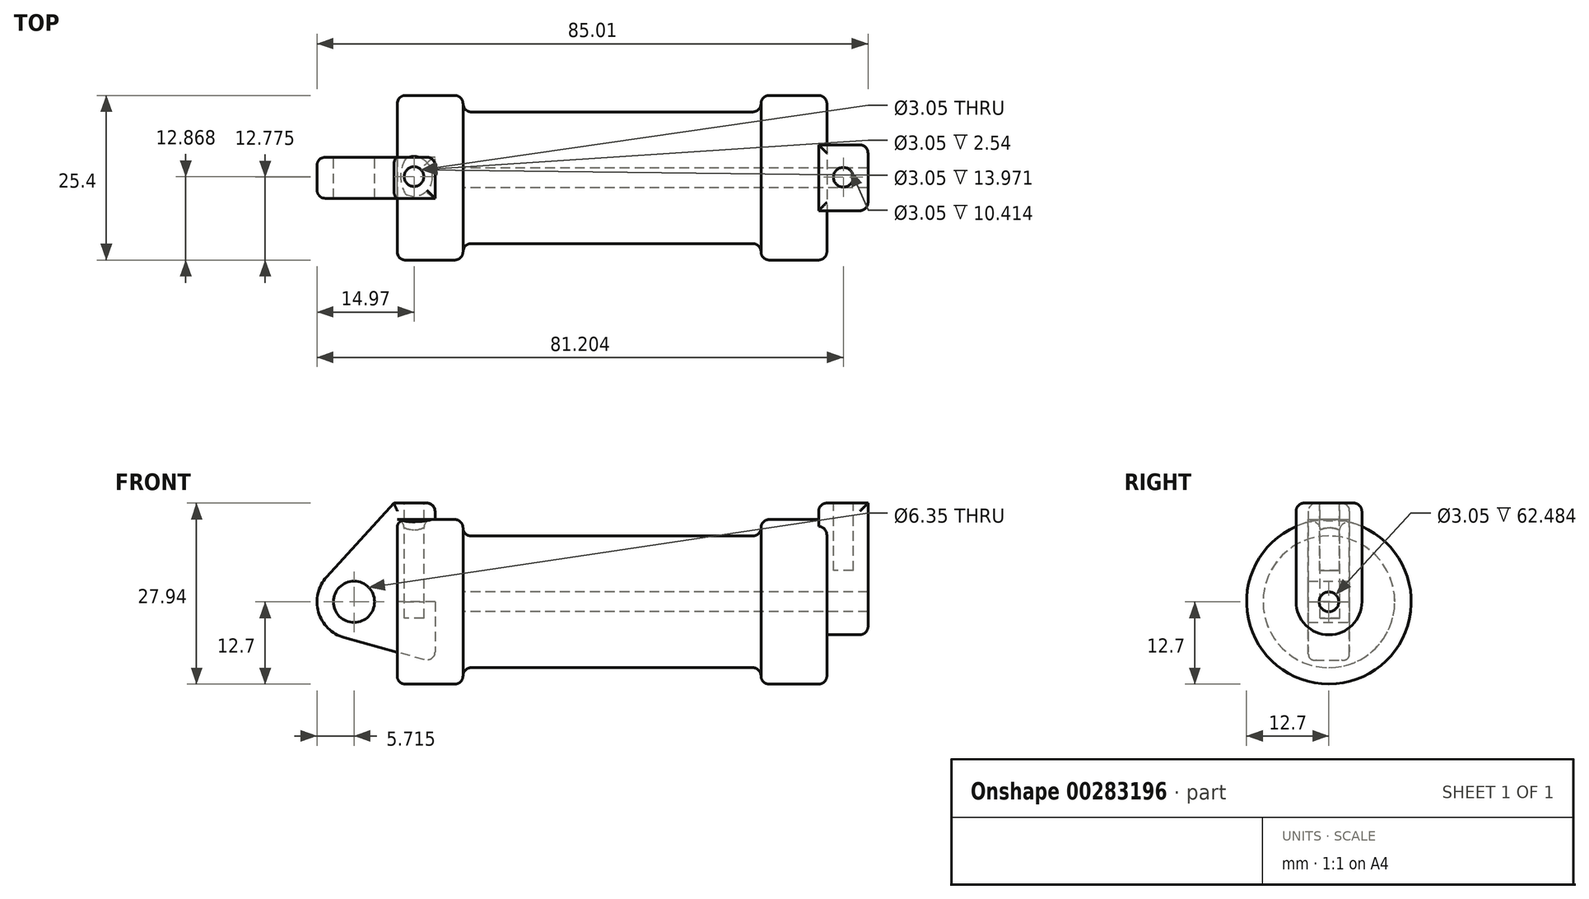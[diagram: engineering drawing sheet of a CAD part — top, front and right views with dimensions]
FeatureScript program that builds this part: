
annotation { "Feature Type Name" : "Feature", "Feature Type Description" : "" }
export const myFeature = defineFeature(function(context is Context, id is Id, definition is map)
    precondition{}
    {
        {
            var Q0;
            Q0=qCreatedBy(makeId("Front.planeOp"),FACE);
            var sketch = newSketch(context, id + "F0", { "sketchPlane" : qUnion([Q0])});
            skLineSegment(sketch, "E0", {"start": v(0, 0) * mm, "end": v(0, 12.7) * mm});
            skLineSegment(sketch, "E1", {"start": v(0, 12.7) * mm, "end": v(10.16, 12.7) * mm});
            skLineSegment(sketch, "E2", {"start": v(10.16, 12.7) * mm, "end": v(10.16, 10.16) * mm});
            skLineSegment(sketch, "E3", {"start": v(10.16, 10.16) * mm, "end": v(56.13, 10.16) * mm});
            skLineSegment(sketch, "E4", {"start": v(56.13, 10.16) * mm, "end": v(56.13, 12.7) * mm});
            skLineSegment(sketch, "E5", {"start": v(56.13, 12.7) * mm, "end": v(66.3, 12.7) * mm});
            skLineSegment(sketch, "E6", {"start": v(66.3, 12.7) * mm, "end": v(66.3, 0) * mm});
            skLineSegment(sketch, "E7", {"start": v(66.3, 0) * mm, "end": v(0, 0) * mm});
            skLineSegment(sketch, "E8", {"start": v(5.84, 15.24) * mm, "end": v(-0.5, 15.24) * mm});
            skLineSegment(sketch, "E9", {"start": v(-0.5, 15.24) * mm, "end": v(-10.88, 3.85) * mm});
            skLineSegment(sketch, "E10", {"start": v(0, 0) * mm, "end": v(-6.65, 0) * mm});
            skCircle(sketch, "E11", {"center": v(-6.65, 0) * mm, "radius": 5.72 * mm});
            skCircle(sketch, "E12", {"center": v(-6.65, 0) * mm, "radius": 3.18 * mm});
            skLineSegment(sketch, "E13", {"start": v(5.84, 15.24) * mm, "end": v(5.84, -9.4) * mm});
            skLineSegment(sketch, "E14", {"start": v(5.84, -9.4) * mm, "end": v(-8.18, -5.5) * mm});
            skSolve(sketch);
        }
        {
            var Q0;
            {var subQ0=sQuery(id+"F0.wireOp",EDGE,"E2");Q0=makeQuery(id+"F0.imprint","IMPRINT",FACE,{"disambiguationData":[TD([[makeQuery(id+"F0.imprint","IMPRINT",EDGE,{"derivedFrom":subQ0}),-1.0]])]});}
            var Q1;
            {var subQ0=sQuery(id+"F0.wireOp",EDGE,"E0");Q1=makeQuery(id+"F0.imprint","IMPRINT",FACE,{"disambiguationData":[TD([[makeQuery(id+"F0.imprint","IMPRINT",EDGE,{"derivedFrom":subQ0}),-1.0]])]});}
            var Q2;
            Q2=sQuery(id+"F0.wireOp",EDGE,"E7");
            revolve(context, id + "F1", {"entities" : qUnion([Q0, Q1]), "axis" : qUnion([Q2]), "revolveType" : RevolveType.FULL});
        }
        {
            var Q0;
            {var subQ1=sQuery(id+"F0.wireOp",EDGE,"E0");Q0=makeQuery(id+"F0.imprint","IMPRINT",FACE,{"disambiguationData":[TD([[makeQuery(id+"F0.imprint","IMPRINT",EDGE,{"derivedFrom":subQ1}),1.0]])]});}
            var Q1;
            Q1=makeQuery(id+"F0.imprint","IMPRINT",FACE,{"disambiguationData":[TD([[makeQuery(id+"F0.imprint","IMPRINT",EDGE,{"derivedFrom":sQuery(id+"F0.wireOp",EDGE,"E12")}),-1.0]])]});
            var Q2;
            {var subQ0=sQuery(id+"F0.wireOp",EDGE,"E14");Q2=makeQuery(id+"F0.imprint","IMPRINT",FACE,{"disambiguationData":[TD([[makeQuery(id+"F0.imprint","IMPRINT",EDGE,{"derivedFrom":subQ0}),-1.0]])]});}
            extrude(context, id + "F2", {"entities" : qUnion([Q0, Q1, Q2]), "endBound" : BoundingType.SYMMETRIC, "depth" : 6.35 * mm});
        }
        {
            var Q0;
            Q0=makeQuery(id+"F1.opRevolve","SWEPT_FACE",FACE,{"disambiguationData":[OSD([sQuery(id+"F0.wireOp",EDGE,"E6")])]});
            var sketch = newSketch(context, id + "F3", { "sketchPlane" : qUnion([Q0])});
            skCircle(sketch, "E15", {"center": v(0, 0) * mm, "radius": 1.52 * mm});
            skCircle(sketch, "E16", {"center": v(0, 0) * mm, "radius": 5.08 * mm});
            skLineSegment(sketch, "E17", {"start": v(-5.08, 0) * mm, "end": v(-5.08, 15.24) * mm});
            skPoint(sketch, "E18.start.orphan", {"position": v(5.08, 0) * mm});
            skLineSegment(sketch, "E19", {"start": v(5.08, 0) * mm, "end": v(5.08, 15.24) * mm});
            skLineSegment(sketch, "E20", {"start": v(-5.08, 15.24) * mm, "end": v(5.08, 15.24) * mm});
            skSolve(sketch);
        }
        {
            var Q0;
            Q0=makeQuery(id+"F3.imprint","IMPRINT",FACE,{"disambiguationData":[TD([[makeQuery(id+"F3.imprint","IMPRINT",EDGE,{"derivedFrom":sQuery(id+"F3.wireOp",EDGE,"E15")}),-1.0]])]});
            var Q1;
            {var subQ0=sQuery(id+"F3.wireOp",EDGE,"E17");var subQ1=sQuery(id+"F3.wireOp",EDGE,"E16");var subQ2=makeQuery(id+"F3.imprint","INTERSECT",VERTEX,{"derivedFrom":[subQ1,subQ0]});Q1=makeQuery(id+"F3.imprint","IMPRINT",FACE,{"disambiguationData":[TD([[makeQuery(id+"F3.imprint","IMPRINT",EDGE,{"disambiguationData":[TD([[subQ2,1.0]])],"derivedFrom":subQ1}),-1.0]])]});}
            var Q2;
            {var subQ0=sQuery(id+"F3.wireOp",EDGE,"E20");Q2=makeQuery(id+"F3.imprint","IMPRINT",FACE,{"disambiguationData":[TD([[makeQuery(id+"F3.imprint","IMPRINT",EDGE,{"derivedFrom":subQ0}),-1.0]])]});}
            extrude(context, id + "F4", {"entities" : qUnion([Q0, Q1, Q2]), "operationType" : NewBodyOperationType.ADD, "depth" : 6.35 * mm});
        }
        {
            var Q0;
            Q0=makeQuery(id+"F4.opExtrude","CAP_FACE",FACE,{"disambiguationData":[OSD([sQuery(id+"F3.wireOp",EDGE,"E15"),sQuery(id+"F3.wireOp",EDGE,"E16"),sQuery(id+"F3.wireOp",EDGE,"E17"),sQuery(id+"F3.wireOp",EDGE,"E19"),sQuery(id+"F3.wireOp",EDGE,"E20")])],"isStart":true});
            extrude(context, id + "F5", {"entities" : qUnion([Q0]), "operationType" : NewBodyOperationType.ADD, "depth" : 1.27 * mm});
        }
        {
            var Q0;
            Q0=makeQuery(id+"F4.boolean.opBoolean","SPLIT",FACE,{"disambiguationData":[TD([makeQuery(id+"F4.opExtrude","SWEPT_FACE",FACE,{"disambiguationData":[OSD([sQuery(id+"F3.wireOp",EDGE,"E15")])]})])],"derivedFrom":makeQuery(id+"F1.opRevolve","SWEPT_FACE",FACE,{"disambiguationData":[OSD([sQuery(id+"F0.wireOp",EDGE,"E6")])]})});
            var Q1;
            Q1=makeQuery(id+"F1.opRevolve","SWEPT_FACE",FACE,{"disambiguationData":[OSD([sQuery(id+"F0.wireOp",EDGE,"E2")])]});
            extrude(context, id + "F6", {"entities" : qUnion([Q0]), "operationType" : NewBodyOperationType.REMOVE, "endBound" : BoundingType.UP_TO_SURFACE, "oppositeDirection" : true, "endBoundEntityFace" : qUnion([Q1]), "depth" : 44.2 * mm});
        }
        {
            var Q0;
            Q0=makeQuery(id+"F2.opExtrude","SWEPT_FACE",FACE,{"disambiguationData":[OSD([sQuery(id+"F0.wireOp",EDGE,"E8")])]});
            var sketch = newSketch(context, id + "F7", { "sketchPlane" : qUnion([Q0])});
            skCircle(sketch, "E21", {"center": v(2.6, 0.17) * mm, "radius": 1.52 * mm});
            skSolve(sketch);
        }
        {
            var Q0;
            {var subQ0=sQuery(id+"F3.wireOp",EDGE,"E20");Q0=makeQuery(id+"F5.boolean.opBoolean","MERGE",FACE,{"derivedFrom":[makeQuery(id+"F4.opExtrude","SWEPT_FACE",FACE,{"disambiguationData":[OSD([subQ0])]}),makeQuery(id+"F5.opExtrude","SWEPT_FACE",FACE,{"disambiguationData":[OSD([subQ0])]})]});}
            var sketch = newSketch(context, id + "F8", { "sketchPlane" : qUnion([Q0])});
            skCircle(sketch, "E22", {"center": v(68.83, 0.08) * mm, "radius": 1.52 * mm});
            skLineSegment(sketch, "E23", {"start": v(68.83, 0) * mm, "end": v(68.83, 0.08) * mm});
            skPoint(sketch, "E24.orphan", {"position": v(68.83, -5.08) * mm});
            skPoint(sketch, "E25.orphan", {"position": v(68.83, 5.08) * mm});
            skPoint(sketch, "E26.orphan", {"position": v(65.02, 0) * mm});
            skPoint(sketch, "E27.end.orphan", {"position": v(72.64, 0) * mm});
            skSolve(sketch);
        }
        {
            var Q0;
            Q0=makeQuery(id+"F7.imprint","IMPRINT",FACE,{"disambiguationData":[TD([[makeQuery(id+"F7.imprint","IMPRINT",EDGE,{"derivedFrom":sQuery(id+"F7.wireOp",EDGE,"E21")}),1.0]])]});
            extrude(context, id + "F9", {"entities" : qUnion([Q0]), "operationType" : NewBodyOperationType.REMOVE, "oppositeDirection" : true, "depth" : 17.78 * mm});
        }
        {
            var Q0;
            {var subQ0=sQuery(id+"F8.wireOp",EDGE,"E22");var subQ1=makeQuery(id+"F5.opExtrude","CAP_EDGE",EDGE,{"disambiguationData":[OSD([sQuery(id+"F3.wireOp",EDGE,"E20")])],"isStart":false});var subQ2=makeQuery(id+"F8.imprint","INTERSECT",VERTEX,{"disambiguationData":[OD(0.0)],"derivedFrom":[subQ1,subQ0]});Q0=makeQuery(id+"F8.imprint","IMPRINT",FACE,{"disambiguationData":[TD([[makeQuery(id+"F8.imprint","IMPRINT",EDGE,{"disambiguationData":[TD([[subQ2,-1.0]])],"derivedFrom":subQ0}),1.0]])]});}
            extrude(context, id + "F10", {"entities" : qUnion([Q0]), "operationType" : NewBodyOperationType.REMOVE, "oppositeDirection" : true, "depth" : 10.4 * mm});
        }
        {
            var Q0;
            {var subQ0=sQuery(id+"F3.wireOp",EDGE,"E20");var subQ1=sQuery(id+"F3.wireOp",EDGE,"E19");Q0=makeQuery(id+"F5.boolean.opBoolean","MERGE",EDGE,{"derivedFrom":[makeQuery(id+"F4.opExtrude","SWEPT_EDGE",EDGE,{"disambiguationData":[OSD([subQ1,subQ0])]}),makeQuery(id+"F5.opExtrude","SWEPT_EDGE",EDGE,{"disambiguationData":[OSD([subQ1,subQ0])]})]});}
            var Q1;
            Q1=makeQuery(id+"F4.opExtrude","CAP_EDGE",EDGE,{"disambiguationData":[OSD([sQuery(id+"F3.wireOp",EDGE,"E19")])],"isStart":false});
            var Q2;
            {var subQ0=sQuery(id+"F3.wireOp",EDGE,"E20");var subQ1=sQuery(id+"F3.wireOp",EDGE,"E17");Q2=makeQuery(id+"F5.boolean.opBoolean","MERGE",EDGE,{"derivedFrom":[makeQuery(id+"F4.opExtrude","SWEPT_EDGE",EDGE,{"disambiguationData":[OSD([subQ1,subQ0])]}),makeQuery(id+"F5.opExtrude","SWEPT_EDGE",EDGE,{"disambiguationData":[OSD([subQ1,subQ0])]})]});}
            var Q3;
            Q3=makeQuery(id+"F5.opExtrude","CAP_EDGE",EDGE,{"disambiguationData":[OSD([sQuery(id+"F3.wireOp",EDGE,"E20")])],"isStart":false});
            var Q4;
            Q4=makeQuery(id+"F4.boolean.opBoolean","SPLIT",EDGE,{"disambiguationData":[OD(1.0)],"derivedFrom":makeQuery(id+"F1.opRevolve","SWEPT_EDGE",EDGE,{"disambiguationData":[OSD([sQuery(id+"F0.wireOp",EDGE,"E5"),sQuery(id+"F0.wireOp",EDGE,"E6")])]})});
            var Q5;
            Q5=makeQuery(id+"F1.opRevolve","SWEPT_EDGE",EDGE,{"disambiguationData":[OSD([sQuery(id+"F0.wireOp",EDGE,"E2"),sQuery(id+"F0.wireOp",EDGE,"E3")])]});
            var Q6;
            {var subQ0=sQuery(id+"F0.wireOp",EDGE,"E13");Q6=makeQuery(id+"F2.opExtrude","CAP_EDGE",EDGE,{"disambiguationData":[OSD([subQ0]),TDD([makeQuery(id+"F0.imprint","IMPRINT",EDGE,{"disambiguationData":[TD([[makeQuery(id+"F0.imprint","INTERSECT",VERTEX,{"derivedFrom":[sQuery(id+"F0.wireOp",EDGE,"E8"),subQ0]}),-1.0]])],"derivedFrom":subQ0})])],"isStart":true});}
            var Q7;
            Q7=makeQuery(id+"F2.opExtrude","CAP_EDGE",EDGE,{"disambiguationData":[OSD([sQuery(id+"F0.wireOp",EDGE,"E8")])],"isStart":true});
            var Q8;
            Q8=makeQuery(id+"F2.opExtrude","CAP_EDGE",EDGE,{"disambiguationData":[OSD([sQuery(id+"F0.wireOp",EDGE,"E14")])],"isStart":true});
            var Q9;
            Q9=makeQuery(id+"F1.opRevolve","SWEPT_EDGE",EDGE,{"disambiguationData":[OSD([sQuery(id+"F0.wireOp",EDGE,"E0"),sQuery(id+"F0.wireOp",EDGE,"E1")])]});
            var Q10;
            Q10=makeQuery(id+"F1.opRevolve","SWEPT_EDGE",EDGE,{"disambiguationData":[OSD([sQuery(id+"F0.wireOp",EDGE,"E4"),sQuery(id+"F0.wireOp",EDGE,"E5")])]});
            var Q11;
            Q11=makeQuery(id+"F1.opRevolve","SWEPT_FACE",FACE,{"disambiguationData":[OSD([sQuery(id+"F0.wireOp",EDGE,"E3")])]});
            var Q12;
            Q12=makeQuery(id+"F1.opRevolve","SWEPT_EDGE",EDGE,{"disambiguationData":[OSD([sQuery(id+"F0.wireOp",EDGE,"E1"),sQuery(id+"F0.wireOp",EDGE,"E2")])]});
            var Q13;
            Q13=makeQuery(id+"F2.opExtrude","SWEPT_FACE",FACE,{"disambiguationData":[OSD([sQuery(id+"F0.wireOp",EDGE,"E14")])]});
            var Q14;
            Q14=makeQuery(id+"F2.opExtrude","CAP_EDGE",EDGE,{"disambiguationData":[OSD([sQuery(id+"F0.wireOp",EDGE,"E8")])],"isStart":false});
            var Q15;
            Q15=makeQuery(id+"F2.opExtrude","SWEPT_EDGE",EDGE,{"disambiguationData":[OSD([sQuery(id+"F0.wireOp",EDGE,"E8"),sQuery(id+"F0.wireOp",EDGE,"E13")])]});
            var Q16;
            Q16=makeQuery(id+"F1.opRevolve","SWEPT_FACE",FACE,{"disambiguationData":[OSD([sQuery(id+"F0.wireOp",EDGE,"E1")])]});
            fillet(context, id + "F11", {"entities" : qUnion([Q0, Q1, Q2, Q3, Q4, Q5, Q6, Q7, Q8, Q9, Q10, Q11, Q12, Q13, Q14, Q15, Q16]), "radius" : 1.27 * mm, "tangentPropagation" : true, "allowEdgeOverflow" : false});
        }
    });
